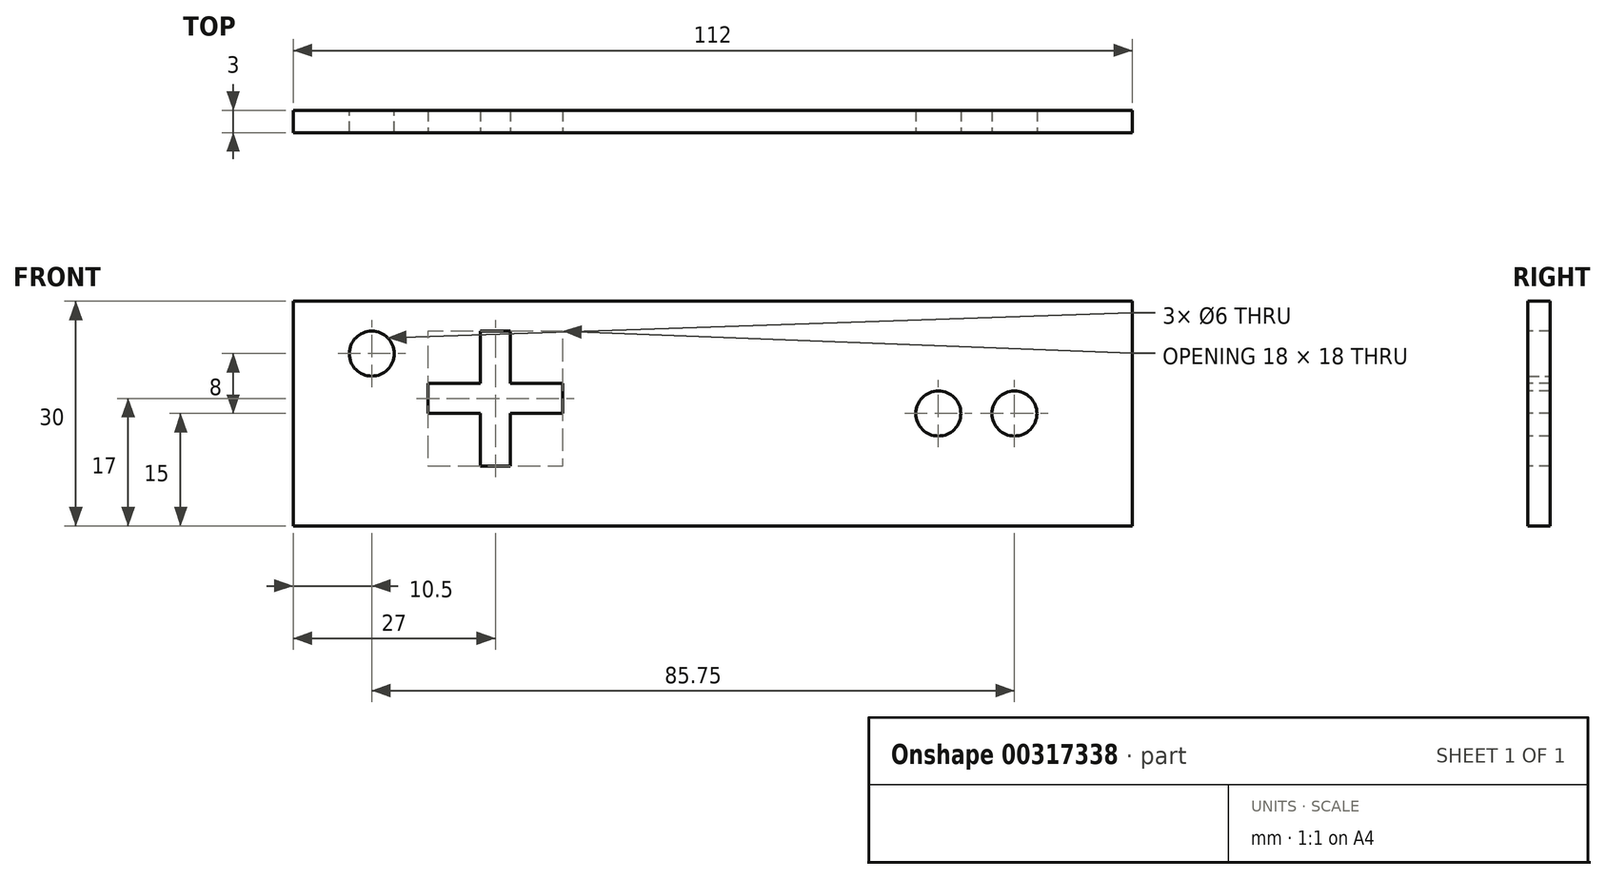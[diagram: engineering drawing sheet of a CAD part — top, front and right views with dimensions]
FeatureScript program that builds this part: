
annotation { "Feature Type Name" : "Feature", "Feature Type Description" : "" }
export const myFeature = defineFeature(function(context is Context, id is Id, definition is map)
    precondition{}
    {
        {
            var Q0;
            Q0=qCreatedBy(makeId("Front.planeOp"),FACE);
            var sketch = newSketch(context, id + "F0", { "sketchPlane" : qUnion([Q0])});
            skLineSegment(sketch, "E0.bottom", {"start": v(56, 15) * mm, "end": v(-56, 15) * mm});
            skLineSegment(sketch, "E0.top", {"start": v(56, -15) * mm, "end": v(-56, -15) * mm});
            skLineSegment(sketch, "E0.left", {"start": v(56, 15) * mm, "end": v(56, -15) * mm});
            skLineSegment(sketch, "E0.right", {"start": v(-56, 15) * mm, "end": v(-56, -15) * mm});
            skPoint(sketch, "E0.middle", {"position": v(0, 0) * mm});
            skLineSegment(sketch, "E1", {"start": v(-56, 15) * mm, "end": v(-56, 8) * mm, "construction": true});
            skLineSegment(sketch, "E2", {"start": v(-56, 8) * mm, "end": v(-45.5, 8) * mm, "construction": true});
            skCircle(sketch, "E3", {"center": v(-45.5, 8) * mm, "radius": 3 * mm});
            skSolve(sketch);
        }
        {
            var Q0;
            Q0=qSketchRegion(id+"F0",true);
            extrude(context, id + "F1", {"entities" : qUnion([Q0]), "depth" : 3 * mm});
        }
        {
            var Q0;
            Q0=makeQuery(id+"F1.opExtrude","CAP_FACE",FACE,{"disambiguationData":[OSD([sQuery(id+"F0.wireOp",EDGE,"E0.bottom"),sQuery(id+"F0.wireOp",EDGE,"E0.top"),sQuery(id+"F0.wireOp",EDGE,"E0.left"),sQuery(id+"F0.wireOp",EDGE,"E0.right"),sQuery(id+"F0.wireOp",EDGE,"E3")])],"isStart":false});
            var sketch = newSketch(context, id + "F2", { "sketchPlane" : qUnion([Q0])});
            skLineSegment(sketch, "E4", {"start": v(-56, 15) * mm, "end": v(-29, 15) * mm, "construction": true});
            skLineSegment(sketch, "E5", {"start": v(-29, 15) * mm, "end": v(-29, 8) * mm, "construction": true});
            skLineSegment(sketch, "E6", {"start": v(-29, 8) * mm, "end": v(-29, -4) * mm, "construction": true});
            skLineSegment(sketch, "E7", {"start": v(-29, 2) * mm, "end": v(-35, 2) * mm, "construction": true});
            skPoint(sketch, "E7.endSnap0", {"position": v(-29, 2) * mm});
            skLineSegment(sketch, "E8", {"start": v(-29, 2) * mm, "end": v(-23, 2) * mm, "construction": true});
            skLineSegment(sketch, "E9", {"start": v(-35, 2) * mm, "end": v(-38, 2) * mm, "construction": true});
            skLineSegment(sketch, "E10", {"start": v(-38, 2) * mm, "end": v(-38, 4) * mm});
            skLineSegment(sketch, "E11.MirrorCS", {"start": v(-38, 2) * mm, "end": v(-38, 0) * mm});
            skLineSegment(sketch, "E12", {"start": v(-29, -4) * mm, "end": v(-29, -7) * mm, "construction": true});
            skLineSegment(sketch, "E13", {"start": v(-29, -7) * mm, "end": v(-31, -7) * mm});
            skLineSegment(sketch, "E14.MirrorCS", {"start": v(-29, -7) * mm, "end": v(-27, -7) * mm});
            skLineSegment(sketch, "E15.MirrorCS", {"start": v(-20, 2) * mm, "end": v(-20, 4) * mm});
            skLineSegment(sketch, "E16.MirrorCS", {"start": v(-20, 2) * mm, "end": v(-20, 0) * mm});
            skLineSegment(sketch, "E17", {"start": v(-38, 0) * mm, "end": v(-31, 0) * mm});
            skLineSegment(sketch, "E18", {"start": v(-31, 0) * mm, "end": v(-31, -7) * mm});
            skLineSegment(sketch, "E19", {"start": v(-27, -7) * mm, "end": v(-27, 0) * mm});
            skLineSegment(sketch, "E20", {"start": v(-27, 0) * mm, "end": v(-20, 0) * mm});
            skLineSegment(sketch, "E21.MirrorCS", {"start": v(-38, 4) * mm, "end": v(-31, 4) * mm});
            skLineSegment(sketch, "E22.MirrorCS", {"start": v(-31, 4) * mm, "end": v(-31, 11) * mm});
            skLineSegment(sketch, "E23.MirrorCS", {"start": v(-27, 11) * mm, "end": v(-27, 4) * mm});
            skLineSegment(sketch, "E24.MirrorCS", {"start": v(-29, 11) * mm, "end": v(-27, 11) * mm});
            skLineSegment(sketch, "E25.MirrorCS", {"start": v(-29, 11) * mm, "end": v(-31, 11) * mm});
            skLineSegment(sketch, "E26.MirrorCS", {"start": v(-27, 4) * mm, "end": v(-20, 4) * mm});
            skSolve(sketch);
        }
        {
            var Q0;
            Q0=qSketchRegion(id+"F2",true);
            extrude(context, id + "F3", {"entities" : qUnion([Q0]), "operationType" : NewBodyOperationType.REMOVE, "oppositeDirection" : true, "depth" : 25 * mm});
        }
        {
            var Q0;
            Q0=makeQuery(id+"F1.opExtrude","CAP_FACE",FACE,{"disambiguationData":[OSD([sQuery(id+"F0.wireOp",EDGE,"E0.bottom"),sQuery(id+"F0.wireOp",EDGE,"E0.top"),sQuery(id+"F0.wireOp",EDGE,"E0.left"),sQuery(id+"F0.wireOp",EDGE,"E0.right"),sQuery(id+"F0.wireOp",EDGE,"E3")])],"isStart":false});
            var sketch = newSketch(context, id + "F4", { "sketchPlane" : qUnion([Q0])});
            skLineSegment(sketch, "E27", {"start": v(56, 15) * mm, "end": v(40.25, 15) * mm, "construction": true});
            skLineSegment(sketch, "E28", {"start": v(40.25, 15) * mm, "end": v(40.25, 0) * mm, "construction": true});
            skLineSegment(sketch, "E29", {"start": v(40.25, 0) * mm, "end": v(30.1, 0) * mm});
            skCircle(sketch, "E30", {"center": v(40.25, 0) * mm, "radius": 3 * mm});
            skCircle(sketch, "E31", {"center": v(30.1, 0) * mm, "radius": 3 * mm});
            skSolve(sketch);
        }
        {
            var Q0;
            Q0=qSketchRegion(id+"F4",true);
            extrude(context, id + "F5", {"entities" : qUnion([Q0]), "operationType" : NewBodyOperationType.REMOVE, "oppositeDirection" : true, "depth" : 25 * mm});
        }
    });
